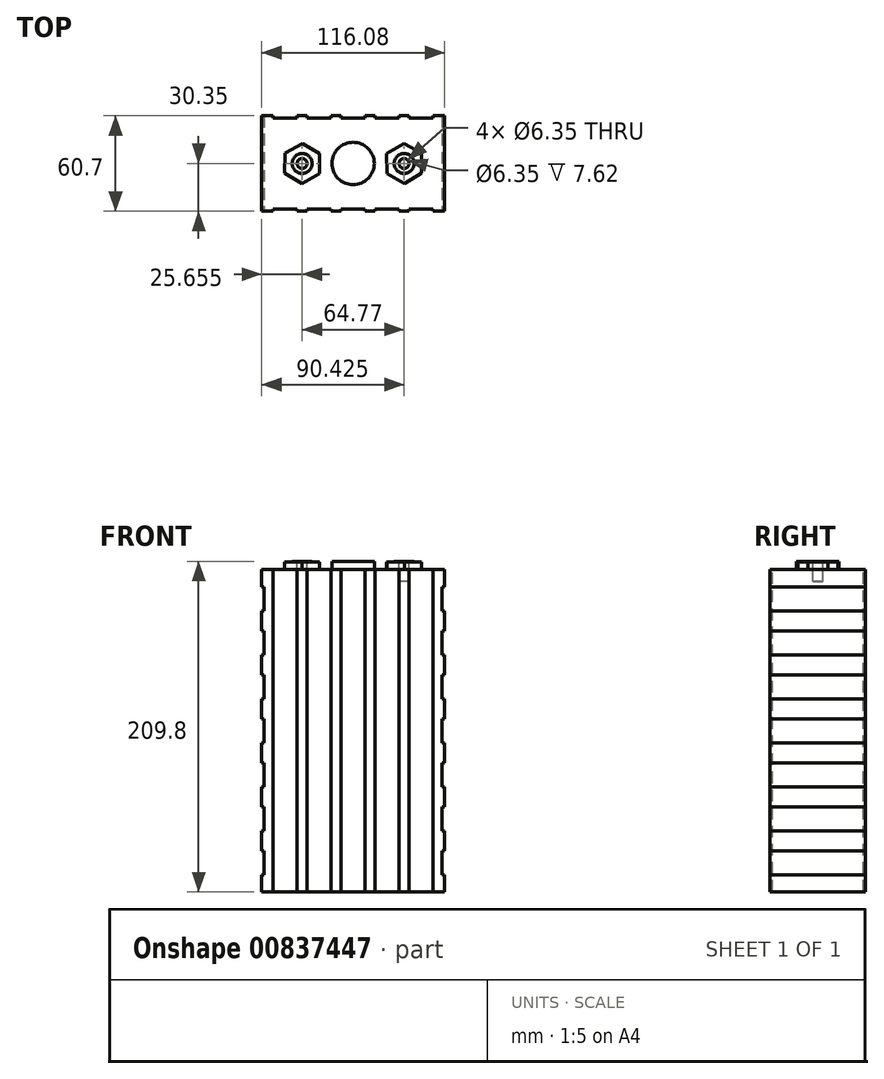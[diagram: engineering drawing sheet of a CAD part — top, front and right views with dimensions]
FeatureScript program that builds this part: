
annotation { "Feature Type Name" : "Feature", "Feature Type Description" : "" }
export const myFeature = defineFeature(function(context is Context, id is Id, definition is map)
    precondition{}
    {
        {
            var Q0;
            Q0=qCreatedBy(makeId("Top.planeOp"),FACE);
            var sketch = newSketch(context, id + "F0", { "sketchPlane" : qUnion([Q0])});
            skLineSegment(sketch, "E0.bottom", {"start": v(-58.04, 30.35) * mm, "end": v(58.04, 30.35) * mm});
            skLineSegment(sketch, "E0.top", {"start": v(-58.04, -30.35) * mm, "end": v(58.04, -30.35) * mm});
            skLineSegment(sketch, "E0.left", {"start": v(-58.04, 30.35) * mm, "end": v(-58.04, -30.35) * mm});
            skLineSegment(sketch, "E0.right", {"start": v(58.04, 30.35) * mm, "end": v(58.04, -30.35) * mm});
            skPoint(sketch, "E0.middle", {"position": v(0, 0) * mm});
            skSolve(sketch);
        }
        {
            var Q0;
            Q0 = qSketchRegion(id + "F0", true);
            extrude(context, id + "F1", {"entities" : qUnion([Q0]), "depth" : 25.4 * mm, "offsetDistance" : 25.4 * mm});
        }
        {
            var Q0;
            Q0=makeQuery(id+"F1.opExtrude","CAP_FACE",FACE,{"disambiguationData":[OSD([sQuery(id+"F0.wireOp",EDGE,"E0.bottom"),sQuery(id+"F0.wireOp",EDGE,"E0.top"),sQuery(id+"F0.wireOp",EDGE,"E0.left"),sQuery(id+"F0.wireOp",EDGE,"E0.right")])],"isStart":false});
            extrude(context, id + "F2", {"entities" : qUnion([Q0]), "operationType" : NewBodyOperationType.ADD, "depth" : 179.32 * mm, "offsetDistance" : 25.4 * mm});
        }
        {
            var Q0;
            Q0=makeQuery(id+"F2.opExtrude","CAP_FACE",FACE,{"disambiguationData":[OSD([sQuery(id+"F0.wireOp",EDGE,"E0.bottom"),sQuery(id+"F0.wireOp",EDGE,"E0.top"),sQuery(id+"F0.wireOp",EDGE,"E0.left"),sQuery(id+"F0.wireOp",EDGE,"E0.right")])],"isStart":false});
            var sketch = newSketch(context, id + "F3", { "sketchPlane" : qUnion([Q0])});
            skLineSegment(sketch, "E1.bottom", {"start": v(-7.62, 30.35) * mm, "end": v(7.62, 30.35) * mm});
            skLineSegment(sketch, "E1.top", {"start": v(-7.62, 28.83) * mm, "end": v(7.62, 28.83) * mm});
            skLineSegment(sketch, "E1.left", {"start": v(-7.62, 30.35) * mm, "end": v(-7.62, 28.83) * mm});
            skLineSegment(sketch, "E1.right", {"start": v(7.62, 30.35) * mm, "end": v(7.62, 28.83) * mm});
            skLineSegment(sketch, "E2.1.0.0", {"start": v(13.97, 30.35) * mm, "end": v(29.2, 30.35) * mm});
            skLineSegment(sketch, "E2.1.0.1", {"start": v(13.97, 28.83) * mm, "end": v(29.21, 28.83) * mm});
            skLineSegment(sketch, "E2.1.0.2", {"start": v(13.97, 30.35) * mm, "end": v(13.97, 28.83) * mm});
            skLineSegment(sketch, "E2.1.0.3", {"start": v(29.21, 30.35) * mm, "end": v(29.21, 28.83) * mm});
            skLineSegment(sketch, "E2.2.0.0", {"start": v(35.56, 30.35) * mm, "end": v(50.8, 30.35) * mm});
            skLineSegment(sketch, "E2.2.0.1", {"start": v(35.56, 28.83) * mm, "end": v(50.8, 28.83) * mm});
            skLineSegment(sketch, "E2.2.0.2", {"start": v(35.56, 30.35) * mm, "end": v(35.56, 28.83) * mm});
            skLineSegment(sketch, "E2.2.0.3", {"start": v(50.8, 30.35) * mm, "end": v(50.8, 28.83) * mm});
            skLineSegment(sketch, "E2.direction1", {"start": v(-7.62, 28.83) * mm, "end": v(13.97, 28.83) * mm, "construction": true});
            skLineSegment(sketch, "E3.1.0.0", {"start": v(-29.21, 30.35) * mm, "end": v(-13.97, 30.35) * mm});
            skLineSegment(sketch, "E3.1.0.1", {"start": v(-29.21, 28.83) * mm, "end": v(-13.97, 28.83) * mm});
            skLineSegment(sketch, "E3.1.0.2", {"start": v(-13.97, 30.35) * mm, "end": v(-13.97, 28.83) * mm});
            skLineSegment(sketch, "E3.1.0.3", {"start": v(-29.2, 30.35) * mm, "end": v(-29.2, 28.83) * mm});
            skLineSegment(sketch, "E3.2.0.0", {"start": v(-50.8, 30.35) * mm, "end": v(-35.56, 30.35) * mm});
            skLineSegment(sketch, "E3.2.0.1", {"start": v(-50.8, 28.83) * mm, "end": v(-35.56, 28.83) * mm});
            skLineSegment(sketch, "E3.2.0.2", {"start": v(-35.56, 30.35) * mm, "end": v(-35.56, 28.83) * mm});
            skLineSegment(sketch, "E3.2.0.3", {"start": v(-50.8, 30.35) * mm, "end": v(-50.8, 28.83) * mm});
            skLineSegment(sketch, "E3.direction1", {"start": v(-7.62, 28.83) * mm, "end": v(-29.2, 28.83) * mm, "construction": true});
            skLineSegment(sketch, "E4", {"start": v(0, 0) * mm, "end": v(-36.99, 0) * mm, "construction": true});
            skLineSegment(sketch, "E5.MirrorCS", {"start": v(-29.2, -30.35) * mm, "end": v(-29.2, -28.83) * mm});
            skLineSegment(sketch, "E6.MirrorCS", {"start": v(7.62, -30.35) * mm, "end": v(7.62, -28.83) * mm});
            skLineSegment(sketch, "E7.MirrorCS", {"start": v(-50.8, -30.35) * mm, "end": v(-50.8, -28.83) * mm});
            skLineSegment(sketch, "E8.MirrorCS", {"start": v(-13.97, -30.35) * mm, "end": v(-13.97, -28.83) * mm});
            skLineSegment(sketch, "E9.MirrorCS", {"start": v(-7.62, -30.35) * mm, "end": v(-7.62, -28.83) * mm});
            skLineSegment(sketch, "E10.MirrorCS", {"start": v(-35.56, -30.35) * mm, "end": v(-35.56, -28.83) * mm});
            skLineSegment(sketch, "E11.MirrorCS", {"start": v(13.97, -30.35) * mm, "end": v(13.97, -28.83) * mm});
            skLineSegment(sketch, "E12.MirrorCS", {"start": v(29.21, -30.35) * mm, "end": v(29.21, -28.83) * mm});
            skLineSegment(sketch, "E13.MirrorCS", {"start": v(50.8, -30.35) * mm, "end": v(50.8, -28.83) * mm});
            skLineSegment(sketch, "E14.MirrorCS", {"start": v(35.56, -30.35) * mm, "end": v(35.56, -28.83) * mm});
            skLineSegment(sketch, "E15.MirrorCS", {"start": v(-29.21, -28.83) * mm, "end": v(-13.97, -28.83) * mm});
            skLineSegment(sketch, "E16.MirrorCS", {"start": v(-7.62, -28.83) * mm, "end": v(7.62, -28.83) * mm});
            skLineSegment(sketch, "E17.MirrorCS", {"start": v(-7.62, -30.35) * mm, "end": v(7.62, -30.35) * mm});
            skLineSegment(sketch, "E18.MirrorCS", {"start": v(-7.62, -28.83) * mm, "end": v(-29.2, -28.83) * mm, "construction": true});
            skLineSegment(sketch, "E19.MirrorCS", {"start": v(-7.62, -28.83) * mm, "end": v(13.97, -28.83) * mm, "construction": true});
            skLineSegment(sketch, "E20.MirrorCS", {"start": v(13.97, -28.83) * mm, "end": v(29.21, -28.83) * mm});
            skLineSegment(sketch, "E21.MirrorCS", {"start": v(35.56, -28.83) * mm, "end": v(50.8, -28.83) * mm});
            skLineSegment(sketch, "E22.MirrorCS", {"start": v(13.97, -30.35) * mm, "end": v(29.2, -30.35) * mm});
            skLineSegment(sketch, "E23.MirrorCS", {"start": v(-50.8, -30.35) * mm, "end": v(-35.56, -30.35) * mm});
            skLineSegment(sketch, "E24.MirrorCS", {"start": v(-50.8, -28.83) * mm, "end": v(-35.56, -28.83) * mm});
            skLineSegment(sketch, "E25.MirrorCS", {"start": v(-29.21, -30.35) * mm, "end": v(-13.97, -30.35) * mm});
            skLineSegment(sketch, "E26.MirrorCS", {"start": v(35.56, -30.35) * mm, "end": v(50.8, -30.35) * mm});
            skSolve(sketch);
        }
        {
            var Q0;
            Q0=makeQuery(id+"F3.imprint","IMPRINT",FACE,{"disambiguationData":[TD([[makeQuery(id+"F3.imprint","IMPRINT",EDGE,{"derivedFrom":sQuery(id+"F3.wireOp",EDGE,"E3.2.0.0")}),-1.0]])]});
            var Q1;
            Q1=makeQuery(id+"F3.imprint","IMPRINT",FACE,{"disambiguationData":[TD([[makeQuery(id+"F3.imprint","IMPRINT",EDGE,{"derivedFrom":sQuery(id+"F3.wireOp",EDGE,"E3.1.0.0")}),-1.0]])]});
            var Q2;
            Q2=makeQuery(id+"F3.imprint","IMPRINT",FACE,{"disambiguationData":[TD([[makeQuery(id+"F3.imprint","IMPRINT",EDGE,{"derivedFrom":sQuery(id+"F3.wireOp",EDGE,"E1.bottom")}),-1.0]])]});
            var Q3;
            Q3=makeQuery(id+"F3.imprint","IMPRINT",FACE,{"disambiguationData":[TD([[makeQuery(id+"F3.imprint","IMPRINT",EDGE,{"derivedFrom":sQuery(id+"F3.wireOp",EDGE,"E2.1.0.0")}),-1.0]])]});
            var Q4;
            Q4=makeQuery(id+"F3.imprint","IMPRINT",FACE,{"disambiguationData":[TD([[makeQuery(id+"F3.imprint","IMPRINT",EDGE,{"derivedFrom":sQuery(id+"F3.wireOp",EDGE,"E2.2.0.0")}),-1.0]])]});
            var Q5;
            Q5=makeQuery(id+"F3.imprint","IMPRINT",FACE,{"disambiguationData":[TD([[makeQuery(id+"F3.imprint","IMPRINT",EDGE,{"derivedFrom":sQuery(id+"F3.wireOp",EDGE,"E13.MirrorCS")}),1.0]])]});
            var Q6;
            Q6=makeQuery(id+"F3.imprint","IMPRINT",FACE,{"disambiguationData":[TD([[makeQuery(id+"F3.imprint","IMPRINT",EDGE,{"derivedFrom":sQuery(id+"F3.wireOp",EDGE,"E11.MirrorCS")}),-1.0]])]});
            var Q7;
            Q7=makeQuery(id+"F3.imprint","IMPRINT",FACE,{"disambiguationData":[TD([[makeQuery(id+"F3.imprint","IMPRINT",EDGE,{"derivedFrom":sQuery(id+"F3.wireOp",EDGE,"E6.MirrorCS")}),1.0]])]});
            var Q8;
            Q8=makeQuery(id+"F3.imprint","IMPRINT",FACE,{"disambiguationData":[TD([[makeQuery(id+"F3.imprint","IMPRINT",EDGE,{"derivedFrom":sQuery(id+"F3.wireOp",EDGE,"E5.MirrorCS")}),-1.0]])]});
            var Q9;
            Q9=makeQuery(id+"F3.imprint","IMPRINT",FACE,{"disambiguationData":[TD([[makeQuery(id+"F3.imprint","IMPRINT",EDGE,{"derivedFrom":sQuery(id+"F3.wireOp",EDGE,"E7.MirrorCS")}),-1.0]])]});
            extrude(context, id + "F4", {"entities" : qUnion([Q0, Q1, Q2, Q3, Q4, Q5, Q6, Q7, Q8, Q9]), "operationType" : NewBodyOperationType.REMOVE, "endBound" : BoundingType.THROUGH_ALL, "oppositeDirection" : true, "depth" : 25.4 * mm, "offsetDistance" : 25.4 * mm});
        }
        {
            var Q0;
            {var subQ0=sQuery(id+"F0.wireOp",EDGE,"E0.left");var subQ2=sQuery(id+"F0.wireOp",EDGE,"E0.top");Q0=makeQuery(id+"F4.boolean.opBoolean","SPLIT",FACE,{"disambiguationData":[TD([makeQuery(id+"F1.opExtrude","SWEPT_FACE",FACE,{"disambiguationData":[OSD([subQ0])]})])],"derivedFrom":makeQuery(id+"F2.boolean.opBoolean","MERGE",FACE,{"derivedFrom":[makeQuery(id+"F1.opExtrude","SWEPT_FACE",FACE,{"disambiguationData":[OSD([subQ2])]}),makeQuery(id+"F2.opExtrude","SWEPT_FACE",FACE,{"disambiguationData":[OSD([subQ2])]})]})});}
            var sketch = newSketch(context, id + "F5", { "sketchPlane" : qUnion([Q0])});
            skLineSegment(sketch, "E27.bottom", {"start": v(-58.04, 94.74) * mm, "end": v(-56.52, 94.74) * mm});
            skLineSegment(sketch, "E27.top", {"start": v(-58.04, 109.98) * mm, "end": v(-56.52, 109.98) * mm});
            skLineSegment(sketch, "E27.left", {"start": v(-58.04, 94.74) * mm, "end": v(-58.04, 109.98) * mm});
            skLineSegment(sketch, "E27.right", {"start": v(-56.52, 94.74) * mm, "end": v(-56.52, 109.98) * mm});
            skLineSegment(sketch, "E28.direction1", {"start": v(-58.04, 95.38) * mm, "end": v(-32.64, 95.38) * mm, "construction": true});
            skLineSegment(sketch, "E28.direction2", {"start": v(-58.04, 95.38) * mm, "end": v(-58.04, 120.78) * mm, "construction": true});
            skLineSegment(sketch, "E29.0.1.0", {"start": v(-58.04, 66.8) * mm, "end": v(-58.04, 82.04) * mm});
            skLineSegment(sketch, "E29.0.1.1", {"start": v(-56.52, 66.8) * mm, "end": v(-56.52, 82.04) * mm});
            skLineSegment(sketch, "E29.0.1.2", {"start": v(-58.04, 82.04) * mm, "end": v(-56.52, 82.04) * mm});
            skLineSegment(sketch, "E29.0.1.3", {"start": v(-58.04, 66.8) * mm, "end": v(-56.52, 66.8) * mm});
            skLineSegment(sketch, "E29.0.2.0", {"start": v(-58.04, 38.86) * mm, "end": v(-58.04, 54.1) * mm});
            skLineSegment(sketch, "E29.0.2.1", {"start": v(-56.52, 38.86) * mm, "end": v(-56.52, 54.1) * mm});
            skLineSegment(sketch, "E29.0.2.2", {"start": v(-58.04, 54.1) * mm, "end": v(-56.52, 54.1) * mm});
            skLineSegment(sketch, "E29.0.2.3", {"start": v(-58.04, 38.86) * mm, "end": v(-56.52, 38.86) * mm});
            skLineSegment(sketch, "E29.0.3.0", {"start": v(-58.04, 10.92) * mm, "end": v(-58.04, 26.16) * mm});
            skLineSegment(sketch, "E29.0.3.1", {"start": v(-56.52, 10.92) * mm, "end": v(-56.52, 26.16) * mm});
            skLineSegment(sketch, "E29.0.3.2", {"start": v(-58.04, 26.16) * mm, "end": v(-56.52, 26.16) * mm});
            skLineSegment(sketch, "E29.0.3.3", {"start": v(-58.04, 10.92) * mm, "end": v(-56.52, 10.92) * mm});
            skLineSegment(sketch, "E29.direction1", {"start": v(-58.04, 94.74) * mm, "end": v(-32.64, 94.74) * mm, "construction": true});
            skLineSegment(sketch, "E29.direction2", {"start": v(-58.04, 94.74) * mm, "end": v(-58.04, 66.8) * mm, "construction": true});
            skLineSegment(sketch, "E30.0.1.0", {"start": v(-56.52, 122.68) * mm, "end": v(-56.52, 137.92) * mm});
            skLineSegment(sketch, "E30.0.1.1", {"start": v(-58.04, 122.68) * mm, "end": v(-58.04, 137.92) * mm});
            skLineSegment(sketch, "E30.0.1.2", {"start": v(-58.04, 137.92) * mm, "end": v(-56.52, 137.92) * mm});
            skLineSegment(sketch, "E30.0.1.3", {"start": v(-58.04, 122.68) * mm, "end": v(-56.52, 122.68) * mm});
            skLineSegment(sketch, "E30.0.2.0", {"start": v(-56.52, 150.62) * mm, "end": v(-56.52, 165.86) * mm});
            skLineSegment(sketch, "E30.0.2.1", {"start": v(-58.04, 150.62) * mm, "end": v(-58.04, 165.86) * mm});
            skLineSegment(sketch, "E30.0.2.2", {"start": v(-58.04, 165.86) * mm, "end": v(-56.52, 165.86) * mm});
            skLineSegment(sketch, "E30.0.2.3", {"start": v(-58.04, 150.62) * mm, "end": v(-56.52, 150.62) * mm});
            skLineSegment(sketch, "E30.0.3.0", {"start": v(-56.52, 178.56) * mm, "end": v(-56.52, 193.8) * mm});
            skLineSegment(sketch, "E30.0.3.1", {"start": v(-58.04, 178.56) * mm, "end": v(-58.04, 193.8) * mm});
            skLineSegment(sketch, "E30.0.3.2", {"start": v(-58.04, 193.8) * mm, "end": v(-56.52, 193.8) * mm});
            skLineSegment(sketch, "E30.0.3.3", {"start": v(-58.04, 178.56) * mm, "end": v(-56.52, 178.56) * mm});
            skLineSegment(sketch, "E30.direction2", {"start": v(-58.04, 94.74) * mm, "end": v(-58.04, 122.68) * mm, "construction": true});
            skLineSegment(sketch, "E31", {"start": v(0, 0) * mm, "end": v(0, 63.7) * mm, "construction": true});
            skLineSegment(sketch, "E32.MirrorCS", {"start": v(58.04, 94.74) * mm, "end": v(56.52, 94.74) * mm});
            skLineSegment(sketch, "E33.MirrorCS", {"start": v(58.04, 66.8) * mm, "end": v(56.52, 66.8) * mm});
            skLineSegment(sketch, "E34.MirrorCS", {"start": v(58.04, 122.68) * mm, "end": v(56.52, 122.68) * mm});
            skLineSegment(sketch, "E35.MirrorCS", {"start": v(58.04, 54.1) * mm, "end": v(56.52, 54.1) * mm});
            skLineSegment(sketch, "E36.MirrorCS", {"start": v(58.04, 193.8) * mm, "end": v(56.52, 193.8) * mm});
            skLineSegment(sketch, "E37.MirrorCS", {"start": v(58.04, 10.92) * mm, "end": v(56.52, 10.92) * mm});
            skLineSegment(sketch, "E38.MirrorCS", {"start": v(58.04, 109.98) * mm, "end": v(56.52, 109.98) * mm});
            skLineSegment(sketch, "E39.MirrorCS", {"start": v(58.04, 165.86) * mm, "end": v(56.52, 165.86) * mm});
            skLineSegment(sketch, "E40.MirrorCS", {"start": v(58.04, 150.62) * mm, "end": v(56.52, 150.62) * mm});
            skLineSegment(sketch, "E41.MirrorCS", {"start": v(58.04, 38.86) * mm, "end": v(56.52, 38.86) * mm});
            skLineSegment(sketch, "E42.MirrorCS", {"start": v(58.04, 26.16) * mm, "end": v(56.52, 26.16) * mm});
            skLineSegment(sketch, "E43.MirrorCS", {"start": v(58.04, 94.74) * mm, "end": v(58.04, 109.98) * mm});
            skLineSegment(sketch, "E44.MirrorCS", {"start": v(58.04, 178.56) * mm, "end": v(56.52, 178.56) * mm});
            skLineSegment(sketch, "E45.MirrorCS", {"start": v(58.04, 82.04) * mm, "end": v(56.52, 82.04) * mm});
            skLineSegment(sketch, "E46.MirrorCS", {"start": v(58.04, 137.92) * mm, "end": v(56.52, 137.92) * mm});
            skLineSegment(sketch, "E47.MirrorCS", {"start": v(58.04, 94.74) * mm, "end": v(58.04, 122.68) * mm, "construction": true});
            skLineSegment(sketch, "E48.MirrorCS", {"start": v(58.04, 66.8) * mm, "end": v(58.04, 82.04) * mm});
            skLineSegment(sketch, "E49.MirrorCS", {"start": v(56.52, 178.56) * mm, "end": v(56.52, 193.8) * mm});
            skLineSegment(sketch, "E50.MirrorCS", {"start": v(56.52, 66.8) * mm, "end": v(56.52, 82.04) * mm});
            skLineSegment(sketch, "E51.MirrorCS", {"start": v(56.52, 122.68) * mm, "end": v(56.52, 137.92) * mm});
            skLineSegment(sketch, "E52.MirrorCS", {"start": v(56.52, 38.86) * mm, "end": v(56.52, 54.1) * mm});
            skLineSegment(sketch, "E53.MirrorCS", {"start": v(56.52, 10.92) * mm, "end": v(56.52, 26.16) * mm});
            skLineSegment(sketch, "E54.MirrorCS", {"start": v(58.04, 10.92) * mm, "end": v(58.04, 26.16) * mm});
            skLineSegment(sketch, "E55.MirrorCS", {"start": v(56.52, 150.62) * mm, "end": v(56.52, 165.86) * mm});
            skLineSegment(sketch, "E56.MirrorCS", {"start": v(58.04, 150.62) * mm, "end": v(58.04, 165.86) * mm});
            skLineSegment(sketch, "E57.MirrorCS", {"start": v(58.04, 122.68) * mm, "end": v(58.04, 137.92) * mm});
            skLineSegment(sketch, "E58.MirrorCS", {"start": v(58.04, 95.38) * mm, "end": v(58.04, 120.78) * mm, "construction": true});
            skLineSegment(sketch, "E59.MirrorCS", {"start": v(58.04, 94.74) * mm, "end": v(58.04, 66.8) * mm, "construction": true});
            skLineSegment(sketch, "E60.MirrorCS", {"start": v(58.04, 38.86) * mm, "end": v(58.04, 54.1) * mm});
            skLineSegment(sketch, "E61.MirrorCS", {"start": v(58.04, 178.56) * mm, "end": v(58.04, 193.8) * mm});
            skLineSegment(sketch, "E62.MirrorCS", {"start": v(56.52, 94.74) * mm, "end": v(56.52, 109.98) * mm});
            skSolve(sketch);
        }
        {
            var Q0;
            Q0 = qSketchRegion(id + "F5", true);
            extrude(context, id + "F6", {"entities" : qUnion([Q0]), "operationType" : NewBodyOperationType.REMOVE, "endBound" : BoundingType.THROUGH_ALL, "oppositeDirection" : true, "depth" : 25.4 * mm, "offsetDistance" : 25.4 * mm});
        }
        {
            var Q0;
            Q0=makeQuery(id+"F2.opExtrude","CAP_FACE",FACE,{"disambiguationData":[OSD([sQuery(id+"F0.wireOp",EDGE,"E0.bottom"),sQuery(id+"F0.wireOp",EDGE,"E0.top"),sQuery(id+"F0.wireOp",EDGE,"E0.left"),sQuery(id+"F0.wireOp",EDGE,"E0.right")])],"isStart":false});
            var sketch = newSketch(context, id + "F7", { "sketchPlane" : qUnion([Q0])});
            skCircle(sketch, "E63", {"center": v(0, 0) * mm, "radius": 13.46 * mm});
            skSolve(sketch);
        }
        {
            var Q0;
            Q0 = qSketchRegion(id + "F7", true);
            extrude(context, id + "F8", {"entities" : qUnion([Q0]), "operationType" : NewBodyOperationType.ADD, "depth" : 5.08 * mm, "offsetDistance" : 25.4 * mm});
        }
        {
            var Q0;
            Q0=makeQuery(id+"F2.opExtrude","CAP_FACE",FACE,{"disambiguationData":[OSD([sQuery(id+"F0.wireOp",EDGE,"E0.bottom"),sQuery(id+"F0.wireOp",EDGE,"E0.top"),sQuery(id+"F0.wireOp",EDGE,"E0.left"),sQuery(id+"F0.wireOp",EDGE,"E0.right")])],"isStart":false});
            var sketch = newSketch(context, id + "F9", { "sketchPlane" : qUnion([Q0])});
            skCircle(sketch, "E64.cCircle", {"center": v(32.39, 0) * mm, "radius": 12.7 * mm, "construction": true});
            skLineSegment(sketch, "E64.0", {"start": v(43.46, -6.21) * mm, "end": v(32.54, -12.7) * mm});
            skLineSegment(sketch, "E64.1", {"start": v(32.54, -12.7) * mm, "end": v(21.47, -6.49) * mm});
            skLineSegment(sketch, "E64.2", {"start": v(21.47, -6.49) * mm, "end": v(21.3, 6.21) * mm});
            skLineSegment(sketch, "E64.3", {"start": v(21.3, 6.21) * mm, "end": v(32.23, 12.7) * mm});
            skLineSegment(sketch, "E64.4", {"start": v(32.23, 12.7) * mm, "end": v(43.3, 6.49) * mm});
            skLineSegment(sketch, "E64.5", {"start": v(43.3, 6.49) * mm, "end": v(43.46, -6.21) * mm});
            skSolve(sketch);
        }
        {
            var Q0;
            Q0 = qSketchRegion(id + "F9", true);
            extrude(context, id + "F10", {"entities" : qUnion([Q0]), "depth" : 4.7 * mm, "offsetDistance" : 25.4 * mm});
        }
        {
            var Q0;
            Q0=makeQuery(id+"F10.opExtrude","CAP_FACE",FACE,{"disambiguationData":[OSD([sQuery(id+"F9.wireOp",EDGE,"E64.0"),sQuery(id+"F9.wireOp",EDGE,"E64.1"),sQuery(id+"F9.wireOp",EDGE,"E64.2"),sQuery(id+"F9.wireOp",EDGE,"E64.3"),sQuery(id+"F9.wireOp",EDGE,"E64.4"),sQuery(id+"F9.wireOp",EDGE,"E64.5")])],"isStart":false});
            var sketch = newSketch(context, id + "F11", { "sketchPlane" : qUnion([Q0])});
            skCircle(sketch, "E65", {"center": v(32.39, 0) * mm, "radius": 6.35 * mm});
            skSolve(sketch);
        }
        {
            var Q0;
            Q0 = qSketchRegion(id + "F11", true);
            extrude(context, id + "F12", {"entities" : qUnion([Q0]), "depth" : 0.38 * mm, "offsetDistance" : 25.4 * mm});
        }
        {
            var Q0;
            Q0=makeQuery(id+"F12.opExtrude","CAP_FACE",FACE,{"disambiguationData":[OSD([sQuery(id+"F11.wireOp",EDGE,"E65")])],"isStart":false});
            var sketch = newSketch(context, id + "F13", { "sketchPlane" : qUnion([Q0])});
            skCircle(sketch, "E66", {"center": v(32.39, 0) * mm, "radius": 3.18 * mm});
            skSolve(sketch);
        }
        {
            var Q0;
            Q0 = qSketchRegion(id + "F13", true);
            extrude(context, id + "F14", {"entities" : qUnion([Q0]), "operationType" : NewBodyOperationType.REMOVE, "oppositeDirection" : true, "depth" : 12.7 * mm, "offsetDistance" : 25.4 * mm});
        }
        {
            var Q0;
            Q0=makeQuery(id+"F12.opExtrude","SWEPT_BODY",BODY,{"disambiguationData":[OSD([sQuery(id+"F11.wireOp",EDGE,"E65")])]});
            var Q1;
            Q1=makeQuery(id+"F10.opExtrude","SWEPT_BODY",BODY,{"disambiguationData":[OSD([sQuery(id+"F9.wireOp",EDGE,"E64.0"),sQuery(id+"F9.wireOp",EDGE,"E64.1"),sQuery(id+"F9.wireOp",EDGE,"E64.2"),sQuery(id+"F9.wireOp",EDGE,"E64.3"),sQuery(id+"F9.wireOp",EDGE,"E64.4"),sQuery(id+"F9.wireOp",EDGE,"E64.5")])]});
            var Q2;
            Q2=qCreatedBy(makeId("Right.planeOp"),FACE);
            mirror(context, id + "F15", {"entities" : qUnion([Q0, Q1]), "mirrorPlane" : qUnion([Q2])});
        }
    });
